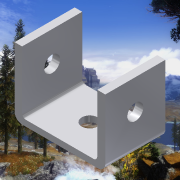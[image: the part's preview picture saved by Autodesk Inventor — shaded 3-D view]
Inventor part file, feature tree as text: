
AUTODESK INVENTOR PART (.ipt)
format: ipt  version: 2015 SP1 (Build 190203100, 203)  size: 166,912 bytes
history: native  units: in
note: dims shown in document units (in); Inventor stores cm internally (conversion verified against a paired STEP export)
features: sketch x4, hole x2, fillet x2, reference x2, extrude x1
ambient origin geometry x8: Origin, YZ Plane, XZ Plane, XY Plane, X Axis, Y Axis, Z Axis, Center Point
bodies: Solid1 (feature_tree)
feature tree (11):
  extrude  "Extrusion1"  Depth=1.125in
  hole  "Hole1"  [1 undecoded]
  hole  "Hole2"  [1 undecoded]
  fillet  "Fillet2"  Radius=0.125in
  fillet  "Fillet3"  Radius=0.0625in
  sketch  "Sketch4"  dims[d10=0.266in d11=0.75in d12=0.507in d13=0.25in d14=0.5635in d15=1.0in d16=0.8108in d17=0.266in d18=0.75in d19=0.507in d20=0.25in d21=0.5635in d22=1.0in d23=0.8108in d24=0.125in d25=0.0625in d26=0.5in d27=0.625in]
  sketch  "Sketch1"  dims[d2=0.125in d3=1.125in]
  sketch  "Sketch2"  dims[d4=1.25in d5=0.1in]
  sketch  "Sketch3"  dims[d6=1.0in d7=0.0in d9=0.5in]
  reference  "Reference2"
  reference  "Reference3"
note: 2 required parameter values undecoded (feature->parameter linkage not recoverable at this tier; creation-order binding heuristic only, values carry confidence <= 0.55)
